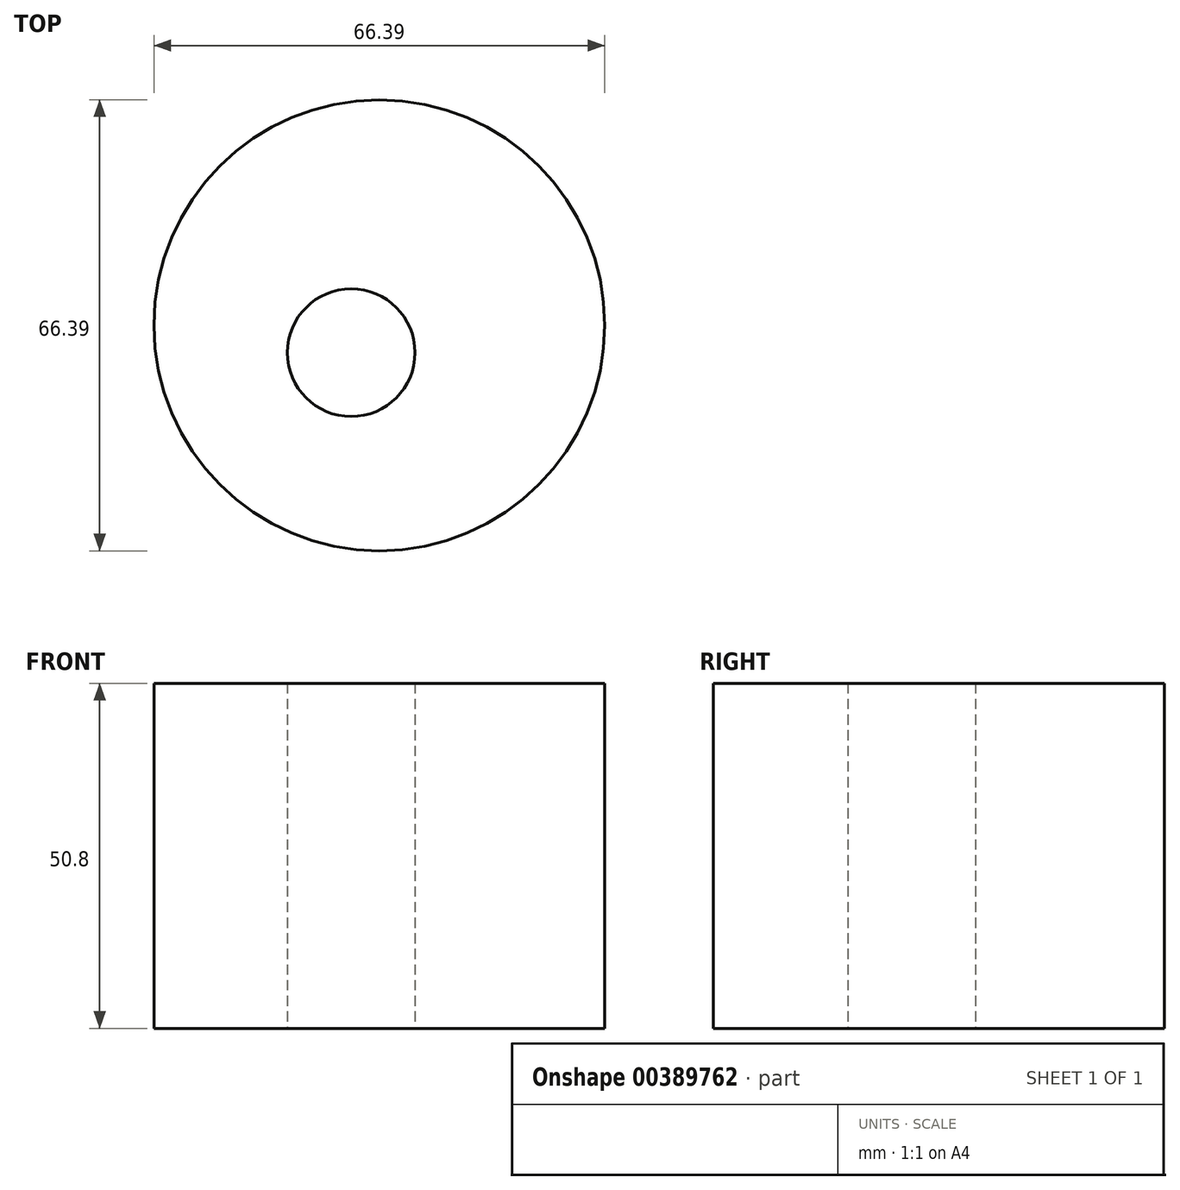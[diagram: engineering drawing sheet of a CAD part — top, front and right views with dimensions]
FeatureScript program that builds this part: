
annotation { "Feature Type Name" : "Feature", "Feature Type Description" : "" }
export const myFeature = defineFeature(function(context is Context, id is Id, definition is map)
    precondition{}
    {
        {
            var Q0;
            Q0=qCreatedBy(makeId("Top.planeOp"),FACE);
            var sketch = newSketch(context, id + "F0", { "sketchPlane" : qUnion([Q0])});
            skCircle(sketch, "E0", {"center": v(-67.6, 74.46) * mm, "radius": 9.4 * mm});
            skCircle(sketch, "E1", {"center": v(-63.45, 78.48) * mm, "radius": 33.2 * mm});
            skSolve(sketch);
        }
        {
            var Q0;
            Q0 = qSketchRegion(id + "F0", true);
            extrude(context, id + "F1", {"entities" : qUnion([Q0]), "depth" : 50.8 * mm});
        }
    });
